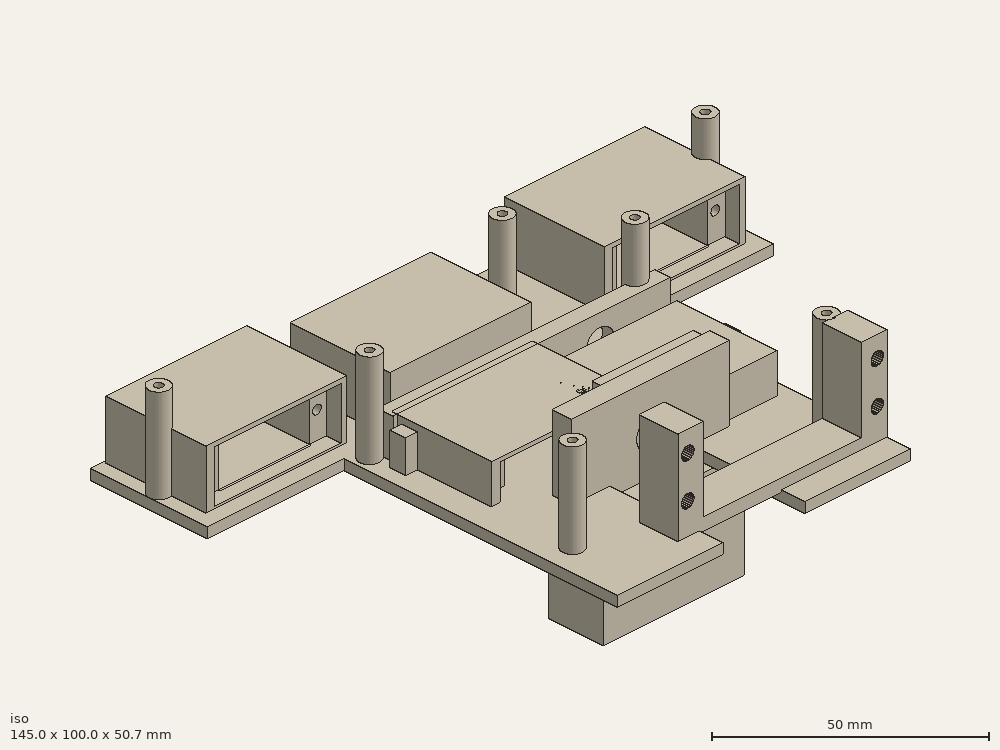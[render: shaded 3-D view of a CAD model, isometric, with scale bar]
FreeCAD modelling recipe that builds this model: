
FCSTD DOCUMENT  (FreeCAD 0.21R33771 (Git))
Label: RobotBrazo
License: All rights reserved
LicenseURL: https://en.wikipedia.org/wiki/All_rights_reserved
objects: PartDesign::Body×27, Sketcher::SketchObject×25, PartDesign::Pad×25, Part::Cut×24, Part::Cylinder×17, Part::MultiFuse×16, Part::FeaturePython×7, Part::Box×6, App::DocumentObjectGroup×5, Part::Feature×3, Mesh::Feature×2, Part::Refine×2, PartDesign::FeatureBase×2, Spreadsheet::Sheet×1
note: 179 computed .brp shape members not serialized (recipe doc carries the construction recipe); baked Part::Feature solids carry a one-line shape summary decoded from their .brp

FEATURE [Mesh::Feature] servo_MG90S
FEATURE [Sketcher::SketchObject] Sketch001
  FullyConstrained = false
  MapMode = 5
  Support = -> [XY_Plane]
  sketch-geometry (4):
    g0: LineSegment StartX=-2.1496 StartY=22.2333 StartZ=0 EndX=33.9123 EndY=22.2333 EndZ=0
    g1: LineSegment StartX=33.9123 StartY=22.2333 StartZ=0 EndX=33.9123 EndY=-3.40604 EndZ=0
    g2: LineSegment StartX=33.9123 StartY=-3.40604 StartZ=0 EndX=-2.1496 EndY=-3.40604 EndZ=0
    g3: LineSegment StartX=-2.1496 StartY=-3.40604 StartZ=0 EndX=-2.1496 EndY=22.2333 EndZ=0
  constraints (8):
    c: Coincident(g0,g1)
    c: Coincident(g1,g2)
    c: Coincident(g2,g3)
    c: Coincident(g3,g0)
    c: Horizontal(g0)
    c: Horizontal(g2)
    c: Vertical(g1)
    c: Vertical(g3)
FEATURE [PartDesign::Pad] Pad
  Direction = (0,0,1)
  Length = 14
  Length2 = 10
  Profile = -> Sketch001
  ReferenceAxis = -> Sketch001 [N_Axis]
  Type = 0
FEATURE [PartDesign::Body] Body  label="Base"
  Group = -> [Sketch001,Pad]
  Origin = -> Origin
  Placement = pos=(0,0,-1) rot=(0,0,1;0rad)
  Tip = -> Pad
FEATURE [Sketcher::SketchObject] Sketch
  FullyConstrained = true
  MapMode = 5
  Placement = pos=(0,0,0) rot=(1,0,0;1.5708rad)
  Support = -> [XZ_Plane003]
  expr: Constraints[10] = Spreadsheet.AnchoCuerpoServo
  expr: Constraints[11] = Spreadsheet.LargoTornillosB
  sketch-geometry (4):
    g0: LineSegment StartX=0 StartY=12.5 StartZ=0 EndX=32.5 EndY=12.5 EndZ=0
    g1: LineSegment StartX=32.5 StartY=12.5 StartZ=0 EndX=32.5 EndY=0 EndZ=0
    g2: LineSegment StartX=32.5 StartY=0 StartZ=0 EndX=0 EndY=0 EndZ=0
    g3: LineSegment StartX=0 StartY=0 StartZ=0 EndX=0 EndY=12.5 EndZ=0
  constraints (12):
    c: Coincident(g0,g1)
    c: Coincident(g1,g2)
    c: Coincident(g2,g3)
    c: Coincident(g3,g0)
    c: Horizontal(g0)
    c: Horizontal(g2)
    c: Vertical(g1)
    c: Vertical(g3)
    c: PointOnObject(g0,g-2)
    c: PointOnObject(g1,g-1)
    c: DistanceY(g1,g1) = 12.5
    c: DistanceX(g0,g0) = 32.5
FEATURE [PartDesign::Pad] Pad001
  Direction = (0,-1,-2e-16)
  Length = 4.5
  Length2 = 10
  Placement = pos=(0,0,0) rot=(1,0,0;1.5708rad)
  Profile = -> Sketch
  ReferenceAxis = -> Sketch [N_Axis]
  Type = 0
  expr: Length = Spreadsheet.AltoServoTor
FEATURE [PartDesign::Body] Body003  label="CorteTornillos"
  Group = -> [Sketch,Pad001]
  Origin = -> Origin003
  Placement = pos=(0,23,0) rot=(0,0,1;0rad)
  Tip = -> Pad001
FEATURE [Part::Cut] Cut  label="BaseCorteTornillos"
  Base = -> Body
  Tool = -> Body003
FEATURE [Sketcher::SketchObject] Sketch002
  FullyConstrained = true
  MapMode = 5
  Placement = pos=(0,0,0) rot=(1,0,0;1.5708rad)
  Support = -> [XZ_Plane004]
  expr: Constraints[10] = Spreadsheet.LargoCuerpoServo
  expr: Constraints[11] = Spreadsheet.DistanciaBaseO
  expr: Constraints[9] = Spreadsheet.AnchoCuerpoServo
  sketch-geometry (4):
    g0: LineSegment StartX=4.75 StartY=12.5 StartZ=0 EndX=28.05 EndY=12.5 EndZ=0
    g1: LineSegment StartX=28.05 StartY=12.5 StartZ=0 EndX=28.05 EndY=0 EndZ=0
    g2: LineSegment StartX=28.05 StartY=0 StartZ=0 EndX=4.75 EndY=0 EndZ=0
    g3: LineSegment StartX=4.75 StartY=0 StartZ=0 EndX=4.75 EndY=12.5 EndZ=0
  constraints (12):
    c: Coincident(g0,g1)
    c: Coincident(g1,g2)
    c: Coincident(g2,g3)
    c: Coincident(g3,g0)
    c: Horizontal(g0)
    c: Horizontal(g2)
    c: Vertical(g1)
    c: Vertical(g3)
    c: PointOnObject(g1,g-1)
    c: DistanceY(g1,g1) = 12.5
    c: DistanceX(g0,g0) = 23.3
    c: DistanceX(g-1,g2) = 4.75
FEATURE [PartDesign::Pad] Pad002
  Direction = (0,-1,-2e-16)
  Length = 19.5
  Length2 = 10
  Placement = pos=(0,0,0) rot=(1,0,0;1.5708rad)
  Profile = -> Sketch002
  ReferenceAxis = -> Sketch002 [N_Axis]
  Type = 0
  expr: Length = Spreadsheet.AltoServo
FEATURE [PartDesign::Body] Body004  label="CorteCuerpo"
  Group = -> [Sketch002,Pad002]
  Origin = -> Origin004
  Placement = pos=(0,19,0) rot=(0,0,1;0rad)
  Tip = -> Pad002
FEATURE [Part::Cut] Cut001  label="SoporteServoMG90S"
  Base = -> Cut
  Tool = -> Body004
FEATURE [Spreadsheet::Sheet] Spreadsheet
  cells = A1='Soporte Servo ; D1='Soporte Servo MG995; A3='AnchoCuerpoServo; B3(AnchoCuerpoServo)=12.5; D3='AnchoCuerpoServo; E3(AnchoCuerpoServoG)=21; A4='LargoCuerpoServo; B4(LargoCuerpoServo)=23.3; D4='LargoCuerpoServo; E4(LargoCuerpoServoG)=40.5; A5='DistanciaBaseO; B5(DistanciaBaseO)=4.75; D5='DistanciaBaseO; E5=4.75; A6='LargoTornillosB; B6(LargoTornillosB)=32.5; D6='LargoTornillosB; E6=32.5; A7='AltoServoTor; B7(AltoServoTor)=4.5; D7='AltoServoTor; E7=4.5; A8='AltoServo; B8(AltoServo)=19.5; D8='AltoServo; E8(AltoServoG)=28; A11='PaloDedoServo; D11='Cuerpo; A12='Largo; B12(PDSLargo)=32; D12='RadioTornillo; E12(CuRadioTornillo)=1; A13='DistaciaCentro; B13(PDSDistanciaCentro)=7; D13='AnchoParedTornillo; E13(CuAnchoParedTornillo)=1.5; A14='DistanciaCurvasPuntas; B14(PDSDistCurvaPunt)=4.5; A15='AnchoPunCen; B15(PDSAnchoPunCen)=6.5; A16='RadioPun; B16(PDSRadioPun)=1.5; A17='Largo Brazo; B17(PDSLargoBrazo)=13; A18='DistaciaComienzoBrazos; B18(PDSDistaComBra)=4.5; A19='DistanciaMitadAlto; B19(PDSDistMidAlto)=3
FEATURE [Part::Cylinder] Cylinder
  Angle = 360
  AttacherType = Attacher::AttachEngine3D
  FirstAngle = 0
  Height = 10
  Placement = pos=(30,22,6) rot=(1,0,0;1.5708rad)
  Radius = 1.1
  SecondAngle = 0
FEATURE [Part::Cylinder] Cylinder001
  Angle = 360
  AttacherType = Attacher::AttachEngine3D
  FirstAngle = 0
  Height = 10
  Placement = pos=(2.2,22,6) rot=(1,0,0;1.5708rad)
  Radius = 1.1
  SecondAngle = 0
FEATURE [Part::MultiFuse] Fusion  label="tornillosSoporteServoHollo"
  Shapes = -> [Cylinder001,Cylinder]
FEATURE [Part::Cut] Cut002  label="SoporteServoCaja"
  Base = -> Cut001
  Placement = pos=(-28.8,27,12) rot=(1,0,0;3.14159rad)
  Tool = -> Fusion
FEATURE [Part::Box] Box  label="Cube"
  AttacherType = Attacher::AttachEngine3D
  Height = 14
  Length = 71
  Placement = pos=(-32,29,-1) rot=(0,0,1;0rad)
  Width = 4
FEATURE [Part::Cylinder] Cylinder004
  Angle = 360
  AttacherType = Attacher::AttachEngine3D
  FirstAngle = 0
  Height = 10
  Placement = pos=(30,22,6) rot=(1,0,0;1.5708rad)
  Radius = 1.1
  SecondAngle = 0
FEATURE [Part::Cylinder] Cylinder005
  Angle = 360
  AttacherType = Attacher::AttachEngine3D
  FirstAngle = 0
  Height = 10
  Placement = pos=(2.2,22,6) rot=(1,0,0;1.5708rad)
  Radius = 1.1
  SecondAngle = 0
FEATURE [Part::MultiFuse] Fusion003  label="tornillosSoporteServoHollo001"
  Shapes = -> [Cylinder005,Cylinder004]
FEATURE [Sketcher::SketchObject] Sketch005
  FullyConstrained = true
  MapMode = 5
  Placement = pos=(0,0,0) rot=(1,0,0;1.5708rad)
  Support = -> [XZ_Plane008]
  expr: Constraints[10] = Spreadsheet.AnchoCuerpoServo
  expr: Constraints[11] = Spreadsheet.LargoTornillosB
  sketch-geometry (4):
    g0: LineSegment StartX=0 StartY=12.5 StartZ=0 EndX=32.5 EndY=12.5 EndZ=0
    g1: LineSegment StartX=32.5 StartY=12.5 StartZ=0 EndX=32.5 EndY=0 EndZ=0
    g2: LineSegment StartX=32.5 StartY=0 StartZ=0 EndX=0 EndY=0 EndZ=0
    g3: LineSegment StartX=0 StartY=0 StartZ=0 EndX=0 EndY=12.5 EndZ=0
  constraints (12):
    c: Coincident(g0,g1)
    c: Coincident(g1,g2)
    c: Coincident(g2,g3)
    c: Coincident(g3,g0)
    c: Horizontal(g0)
    c: Horizontal(g2)
    c: Vertical(g1)
    c: Vertical(g3)
    c: PointOnObject(g0,g-2)
    c: PointOnObject(g1,g-1)
    c: DistanceY(g1,g1) = 12.5
    c: DistanceX(g0,g0) = 32.5
FEATURE [PartDesign::Pad] Pad006
  Direction = (0,-1,-2e-16)
  Length = 4.5
  Length2 = 10
  Placement = pos=(0,0,0) rot=(1,0,0;1.5708rad)
  Profile = -> Sketch005
  ReferenceAxis = -> Sketch005 [N_Axis]
  Type = 0
  expr: Length = Spreadsheet.AltoServoTor
FEATURE [PartDesign::Body] Body008  label="CorteTornillos001"
  Group = -> [Sketch005,Pad006]
  Origin = -> Origin008
  Placement = pos=(0,23,0) rot=(0,0,1;0rad)
  Tip = -> Pad006
FEATURE [Sketcher::SketchObject] Sketch006
  FullyConstrained = false
  MapMode = 5
  Support = -> [XY_Plane007]
  sketch-geometry (4):
    g0: LineSegment StartX=-2.1496 StartY=22.2333 StartZ=0 EndX=33.9123 EndY=22.2333 EndZ=0
    g1: LineSegment StartX=33.9123 StartY=22.2333 StartZ=0 EndX=33.9123 EndY=-3.40604 EndZ=0
    g2: LineSegment StartX=33.9123 StartY=-3.40604 StartZ=0 EndX=-2.1496 EndY=-3.40604 EndZ=0
    g3: LineSegment StartX=-2.1496 StartY=-3.40604 StartZ=0 EndX=-2.1496 EndY=22.2333 EndZ=0
  constraints (8):
    c: Coincident(g0,g1)
    c: Coincident(g1,g2)
    c: Coincident(g2,g3)
    c: Coincident(g3,g0)
    c: Horizontal(g0)
    c: Horizontal(g2)
    c: Vertical(g1)
    c: Vertical(g3)
FEATURE [PartDesign::Pad] Pad005
  Direction = (0,0,1)
  Length = 14
  Length2 = 10
  Profile = -> Sketch006
  ReferenceAxis = -> Sketch006 [N_Axis]
  Type = 0
FEATURE [PartDesign::Body] Body007  label="Base001"
  Group = -> [Sketch006,Pad005]
  Origin = -> Origin007
  Placement = pos=(0,0,-1) rot=(0,0,1;0rad)
  Tip = -> Pad005
FEATURE [Part::Cut] Cut003  label="BaseCorteTornillos001"
  Base = -> Body007
  Tool = -> Body008
FEATURE [Sketcher::SketchObject] Sketch007
  FullyConstrained = true
  MapMode = 5
  Placement = pos=(0,0,0) rot=(1,0,0;1.5708rad)
  Support = -> [XZ_Plane009]
  expr: Constraints[10] = Spreadsheet.LargoCuerpoServo
  expr: Constraints[11] = Spreadsheet.DistanciaBaseO
  expr: Constraints[9] = Spreadsheet.AnchoCuerpoServo
  sketch-geometry (4):
    g0: LineSegment StartX=4.75 StartY=12.5 StartZ=0 EndX=28.05 EndY=12.5 EndZ=0
    g1: LineSegment StartX=28.05 StartY=12.5 StartZ=0 EndX=28.05 EndY=0 EndZ=0
    g2: LineSegment StartX=28.05 StartY=0 StartZ=0 EndX=4.75 EndY=0 EndZ=0
    g3: LineSegment StartX=4.75 StartY=0 StartZ=0 EndX=4.75 EndY=12.5 EndZ=0
  constraints (12):
    c: Coincident(g0,g1)
    c: Coincident(g1,g2)
    c: Coincident(g2,g3)
    c: Coincident(g3,g0)
    c: Horizontal(g0)
    c: Horizontal(g2)
    c: Vertical(g1)
    c: Vertical(g3)
    c: PointOnObject(g1,g-1)
    c: DistanceY(g1,g1) = 12.5
    c: DistanceX(g0,g0) = 23.3
    c: DistanceX(g-1,g2) = 4.75
FEATURE [PartDesign::Pad] Pad007
  Direction = (0,-1,-2e-16)
  Length = 19.5
  Length2 = 10
  Placement = pos=(0,0,0) rot=(1,0,0;1.5708rad)
  Profile = -> Sketch007
  ReferenceAxis = -> Sketch007 [N_Axis]
  Type = 0
  expr: Length = Spreadsheet.AltoServo
FEATURE [PartDesign::Body] Body009  label="CorteCuerpo001"
  Group = -> [Sketch007,Pad007]
  Origin = -> Origin009
  Placement = pos=(0,19,0) rot=(0,0,1;0rad)
  Tip = -> Pad007
FEATURE [Part::Cut] Cut004  label="SoporteServoMG90S001"
  Base = -> Cut003
  Tool = -> Body009
FEATURE [Part::Cylinder] Cylinder006
  Angle = 360
  AttacherType = Attacher::AttachEngine3D
  FirstAngle = 0
  Height = 4
  Placement = pos=(-20,35,6) rot=(0,0.707107,-0.707107;3.14159rad)
  Radius = 5
  SecondAngle = 0
FEATURE [Sketcher::SketchObject] Sketch009
  FullyConstrained = false
  MapMode = 5
  Placement = pos=(0,0,0) rot=(0.57735,0.57735,0.57735;2.0944rad)
  Support = -> [YZ_Plane011]
  sketch-geometry (4):
    g0: LineSegment StartX=24.8013 StartY=11.4231 StartZ=0 EndX=28.8013 EndY=11.4231 EndZ=0
    g1: LineSegment StartX=28.8013 StartY=11.4231 StartZ=0 EndX=28.8013 EndY=0 EndZ=0
    g2: LineSegment StartX=28.8013 StartY=0 StartZ=0 EndX=24.8013 EndY=0 EndZ=0
    g3: LineSegment StartX=24.8013 StartY=0 StartZ=0 EndX=24.8013 EndY=11.4231 EndZ=0
  constraints (10):
    c: Coincident(g0,g1)
    c: Coincident(g1,g2)
    c: Coincident(g2,g3)
    c: Coincident(g3,g0)
    c: Horizontal(g0)
    c: Horizontal(g2)
    c: Vertical(g1)
    c: Vertical(g3)
    c: PointOnObject(g1,g-1)
    c: DistanceX(g2,g2) = 4
FEATURE [PartDesign::Pad] Pad009
  Direction = (1,-2e-16,3e-16)
  Length = 10
  Length2 = 10
  Placement = pos=(0,0,0) rot=(0.57735,0.57735,0.57735;2.0944rad)
  Profile = -> Sketch009
  ReferenceAxis = -> Sketch009 [N_Axis]
  Type = 0
FEATURE [PartDesign::Body] Body011  label="corte cables"
  Group = -> [Sketch009,Pad009]
  Origin = -> Origin011
  Placement = pos=(-34,-1,0) rot=(0,0,1;0rad)
  Tip = -> Pad009
FEATURE [Part::Cut] Cut005  label="SoporteServoCajaMG90S"
  Base = -> Cut004
  Tool = -> Fusion003
FEATURE [App::DocumentObjectGroup] Group002  label="Hombro"
FEATURE [Part::Box] Box001  label="Cube001"
  AttacherType = Attacher::AttachEngine3D
  Height = 14
  Length = 38
  Placement = pos=(0,10,-4) rot=(0,0,1;0rad)
  Width = 4
FEATURE [Part::Cylinder] Cylinder010
  Angle = 360
  AttacherType = Attacher::AttachEngine3D
  FirstAngle = 0
  Height = 8
  Placement = pos=(21,34,6.3) rot=(0.999009,0.030969,-0.031968;1.5708rad)
  Radius = 3.6
  SecondAngle = 0
FEATURE [Sketcher::SketchObject] Sketch013
  FullyConstrained = false
  MapMode = 5
  Placement = pos=(0,0,0) rot=(1,0,0;1.5708rad)
  Support = -> [XZ_Plane015]
  expr: Constraints[13] = Spreadsheet.PDSLargo
  expr: Constraints[20] = Spreadsheet.PDSLargo / 2
  expr: Constraints[25] = Spreadsheet.PDSAnchoPunCen
  sketch-geometry (15):
    g0: GeomPoint X=-8e-15 Y=0.00495753 Z=0
    g1: GeomPoint X=-2.07359 Y=3.25 Z=0
    g2: GeomPoint X=-2.07359 Y=-3.25 Z=0
    g3: GeomPoint X=2.07359 Y=3.25 Z=0
    g4: GeomPoint X=2.07359 Y=-3.25 Z=0
    g5: ArcOfCircle CenterX=-18 CenterY=-1.72e-14 CenterZ=0 NormalX=0 NormalY=0 NormalZ=1 AngleXU=0 Radius=2 StartAngle=1.57081 EndAngle=4.71238
    g6: LineSegment StartX=-18 StartY=2 StartZ=0 EndX=-2.07359 EndY=3.25 EndZ=0
    g7: LineSegment StartX=-18 StartY=-2 StartZ=0 EndX=-2.07359 EndY=-3.25 EndZ=0
    g8: LineSegment StartX=2.07359 StartY=3.25 StartZ=0 EndX=18 EndY=2 EndZ=0
    g9: LineSegment StartX=2.07359 StartY=-3.25 StartZ=0 EndX=18 EndY=-2 EndZ=0
    g10: ArcOfCircle CenterX=18 CenterY=1.72e-14 CenterZ=0 NormalX=0 NormalY=0 NormalZ=1 AngleXU=0 Radius=2 StartAngle=4.7124 EndAngle=7.85397
    g11: ArcOfCircle CenterX=-8e-15 CenterY=0.00495753 CenterZ=0 NormalX=0 NormalY=0 NormalZ=1 AngleXU=0 Radius=3.85934 StartAngle=4.14517 EndAngle=5.27961
    g12: ArcOfCircle CenterX=0 CenterY=0.0440704 CenterZ=0 NormalX=0 NormalY=0 NormalZ=1 AngleXU=0 Radius=3.81808 StartAngle=0.996676 EndAngle=2.14492
    g13: GeomPoint X=-16 Y=0 Z=0
    g14: GeomPoint X=16 Y=-1.65466e-05 Z=0
  constraints (29):
    c: Coincident(g6,g5)
    c: Coincident(g6,g1)
    c: Coincident(g7,g5)
    c: Coincident(g7,g2)
    c: Coincident(g8,g3)
    c: Coincident(g9,g4)
    c: Symmetric(g5,g5,g-1)
    c: Coincident(g10,g8)
    c: Coincident(g10,g9)
    c: Symmetric(g8,g9,g-1)
    c: Equal(g5,g10)
    c: PointOnObject(g13,g5)
    c: PointOnObject(g14,g10)
    c: DistanceX(g13,g14) = 32
    c: Coincident(g8,g12)
    c: Coincident(g1,g12)
    c: Symmetric(g8,g6,g-2)
    c: Coincident(g11,g0)
    c: DistanceY(g9,g8) = 6.5
    c: Radius(g5) = 2
    c: DistanceX(g13,g11) = 16
    c: Coincident(g7,g11)
    c: Coincident(g11,g9)
    c: Symmetric(g7,g9,g-2)
    c: Symmetric(g7,g6,g-1)
    c: DistanceY(g7,g6) = 6.5
    c: DistanceY(g5,g5) = 4
    c: Symmetric(g8,g5,g-2)
    c: PointOnObject(g13,g-1)
FEATURE [PartDesign::Pad] Pad013
  Direction = (0,-1,-2e-16)
  Length = 3
  Length2 = 10
  Placement = pos=(0,0,0) rot=(1,0,0;1.5708rad)
  Profile = -> Sketch013
  ReferenceAxis = -> Sketch013 [N_Axis]
  Type = 0
FEATURE [PartDesign::Body] Body015  label="aggarre004"
  Group = -> [Sketch013,Pad013]
  Origin = -> Origin015
  Placement = pos=(21,35,6.3) rot=(0,0,1;0rad)
  Tip = -> Pad013
FEATURE [Part::MultiFuse] Fusion009  label="ServoAgarre004"
  Shapes = -> [Body015,Cylinder010]
FEATURE [Part::Cut] Cut011
  Base = -> Box
  Tool = -> Cylinder006
FEATURE [Part::Cut] Cut012
  Base = -> Cut011
  Tool = -> Fusion009
FEATURE [Part::MultiFuse] Fusion010
  Shapes = -> [Cut012,Cut002]
FEATURE [App::DocumentObjectGroup] Group  label="GarraSoporte"
  Group = -> [Fusion010,Body011]
FEATURE [Part::Box] Box002  label="Cube002"
  AttacherType = Attacher::AttachEngine3D
  Height = 5
  Length = 38
  Placement = pos=(0,-9,-8) rot=(0,0,1;0rad)
  Width = 23
FEATURE [Sketcher::SketchObject] Sketch016
  FullyConstrained = true
  MapMode = 5
  Support = -> [XY_Plane018]
  sketch-geometry (8):
    g0: LineSegment StartX=-72.5 StartY=36 StartZ=0 EndX=-72.5 EndY=66 EndZ=0
    g1: LineSegment StartX=-72.5 StartY=66 StartZ=0 EndX=72.5 EndY=66 EndZ=0
    g2: LineSegment StartX=72.5 StartY=66 StartZ=0 EndX=72.5 EndY=36 EndZ=0
    g3: LineSegment StartX=-37.5 StartY=36 StartZ=0 EndX=-37.5 EndY=-34 EndZ=0
    g4: LineSegment StartX=-72.5 StartY=36 StartZ=0 EndX=-37.5 EndY=36 EndZ=0
    g5: LineSegment StartX=72.5 StartY=36 StartZ=0 EndX=37.5 EndY=36 EndZ=0
    g6: LineSegment StartX=37.5 StartY=36 StartZ=0 EndX=37.5 EndY=-34 EndZ=0
    g7: LineSegment StartX=-37.5 StartY=-34 StartZ=0 EndX=37.5 EndY=-34 EndZ=0
  constraints (22):
    c: Vertical(g0)
    c: Coincident(g4,g0)
    c: Coincident(g4,g3)
    c: Horizontal(g4)
    c: Horizontal(g5)
    c: Coincident(g6,g5)
    c: Symmetric(g7,g7,g-2)
    c: DistanceY(g2,g2) = 30
    c: Coincident(g6,g7)
    c: Coincident(g3,g7)
    c: DistanceX(g7,g7) = 75
    c: DistanceX(g3,g5) = 75
    c: Symmetric(g5,g3,g-2)
    c: DistanceY(g6,g6) = 70
    c: Equal(g0,g2)
    c: Coincident(g1,g0)
    c: Coincident(g2,g5)
    c: Coincident(g1,g2)
    c: Equal(g5,g4)
    c: DistanceX(g5,g5) = 35
    c: Vertical(g2)
    c: DistanceY(g-1,g0) = 66
FEATURE [PartDesign::Pad] Pad016
  Direction = (0,0,1)
  Length = 2.5
  Length2 = 10
  Profile = -> Sketch016
  ReferenceAxis = -> Sketch016 [N_Axis]
  Type = 0
FEATURE [PartDesign::Body] Body018  label="CuerpoBase"
  Group = -> [Sketch016,Pad016]
  Origin = -> Origin018
  Placement = pos=(0,0,1) rot=(0,0,1;0rad)
  Tip = -> Pad016
FEATURE [Mesh::Feature] ServoGarra_8_  label="ServoGarra(8)"
  Placement = pos=(40,-74,3) rot=(0,0,1;0rad)
FEATURE [Part::Cylinder] Cylinder013
  Angle = 360
  AttacherType = Attacher::AttachEngine3D
  FirstAngle = 0
  Height = 10
  Placement = pos=(30,22,6) rot=(1,0,0;1.5708rad)
  Radius = 1.1
  SecondAngle = 0
FEATURE [Part::Cylinder] Cylinder014
  Angle = 360
  AttacherType = Attacher::AttachEngine3D
  FirstAngle = 0
  Height = 10
  Placement = pos=(2.2,22,6) rot=(1,0,0;1.5708rad)
  Radius = 1.1
  SecondAngle = 0
FEATURE [Part::MultiFuse] Fusion014  label="tornillosSoporteServoHollo002"
  Shapes = -> [Cylinder014,Cylinder013]
FEATURE [Sketcher::SketchObject] Sketch017
  FullyConstrained = true
  MapMode = 5
  Placement = pos=(0,0,0) rot=(1,0,0;1.5708rad)
  Support = -> [XZ_Plane020]
  expr: Constraints[10] = Spreadsheet.AnchoCuerpoServo
  expr: Constraints[11] = Spreadsheet.LargoTornillosB
  sketch-geometry (4):
    g0: LineSegment StartX=0 StartY=12.5 StartZ=0 EndX=32.5 EndY=12.5 EndZ=0
    g1: LineSegment StartX=32.5 StartY=12.5 StartZ=0 EndX=32.5 EndY=0 EndZ=0
    g2: LineSegment StartX=32.5 StartY=0 StartZ=0 EndX=0 EndY=0 EndZ=0
    g3: LineSegment StartX=0 StartY=0 StartZ=0 EndX=0 EndY=12.5 EndZ=0
  constraints (12):
    c: Coincident(g0,g1)
    c: Coincident(g1,g2)
    c: Coincident(g2,g3)
    c: Coincident(g3,g0)
    c: Horizontal(g0)
    c: Horizontal(g2)
    c: Vertical(g1)
    c: Vertical(g3)
    c: PointOnObject(g0,g-2)
    c: PointOnObject(g1,g-1)
    c: DistanceY(g1,g1) = 12.5
    c: DistanceX(g0,g0) = 32.5
FEATURE [PartDesign::Pad] Pad018
  Direction = (0,-1,-2e-16)
  Length = 4.5
  Length2 = 10
  Placement = pos=(0,0,0) rot=(1,0,0;1.5708rad)
  Profile = -> Sketch017
  ReferenceAxis = -> Sketch017 [N_Axis]
  Type = 0
  expr: Length = Spreadsheet.AltoServoTor
FEATURE [PartDesign::Body] Body020  label="CorteTornillos002"
  Group = -> [Sketch017,Pad018]
  Origin = -> Origin020
  Placement = pos=(0,23,0) rot=(0,0,1;0rad)
  Tip = -> Pad018
FEATURE [Sketcher::SketchObject] Sketch018
  FullyConstrained = false
  MapMode = 5
  Support = -> [XY_Plane019]
  sketch-geometry (4):
    g0: LineSegment StartX=-2.1496 StartY=22.2333 StartZ=0 EndX=33.9123 EndY=22.2333 EndZ=0
    g1: LineSegment StartX=33.9123 StartY=22.2333 StartZ=0 EndX=33.9123 EndY=-3.40604 EndZ=0
    g2: LineSegment StartX=33.9123 StartY=-3.40604 StartZ=0 EndX=-2.1496 EndY=-3.40604 EndZ=0
    g3: LineSegment StartX=-2.1496 StartY=-3.40604 StartZ=0 EndX=-2.1496 EndY=22.2333 EndZ=0
  constraints (8):
    c: Coincident(g0,g1)
    c: Coincident(g1,g2)
    c: Coincident(g2,g3)
    c: Coincident(g3,g0)
    c: Horizontal(g0)
    c: Horizontal(g2)
    c: Vertical(g1)
    c: Vertical(g3)
FEATURE [PartDesign::Pad] Pad017
  Direction = (0,0,1)
  Length = 14
  Length2 = 10
  Profile = -> Sketch018
  ReferenceAxis = -> Sketch018 [N_Axis]
  Type = 0
FEATURE [PartDesign::Body] Body019  label="Base002"
  Group = -> [Sketch018,Pad017]
  Origin = -> Origin019
  Placement = pos=(0,0,-1) rot=(0,0,1;0rad)
  Tip = -> Pad017
FEATURE [Part::Cut] Cut014  label="BaseCorteTornillos002"
  Base = -> Body019
  Tool = -> Body020
FEATURE [Sketcher::SketchObject] Sketch019
  FullyConstrained = true
  MapMode = 5
  Placement = pos=(0,0,0) rot=(1,0,0;1.5708rad)
  Support = -> [XZ_Plane021]
  expr: Constraints[10] = Spreadsheet.LargoCuerpoServo
  expr: Constraints[11] = Spreadsheet.DistanciaBaseO
  expr: Constraints[9] = Spreadsheet.AnchoCuerpoServo
  sketch-geometry (4):
    g0: LineSegment StartX=4.75 StartY=12.5 StartZ=0 EndX=28.05 EndY=12.5 EndZ=0
    g1: LineSegment StartX=28.05 StartY=12.5 StartZ=0 EndX=28.05 EndY=0 EndZ=0
    g2: LineSegment StartX=28.05 StartY=0 StartZ=0 EndX=4.75 EndY=0 EndZ=0
    g3: LineSegment StartX=4.75 StartY=0 StartZ=0 EndX=4.75 EndY=12.5 EndZ=0
  constraints (12):
    c: Coincident(g0,g1)
    c: Coincident(g1,g2)
    c: Coincident(g2,g3)
    c: Coincident(g3,g0)
    c: Horizontal(g0)
    c: Horizontal(g2)
    c: Vertical(g1)
    c: Vertical(g3)
    c: PointOnObject(g1,g-1)
    c: DistanceY(g1,g1) = 12.5
    c: DistanceX(g0,g0) = 23.3
    c: DistanceX(g-1,g2) = 4.75
FEATURE [PartDesign::Pad] Pad019
  Direction = (0,-1,-2e-16)
  Length = 19.5
  Length2 = 10
  Placement = pos=(0,0,0) rot=(1,0,0;1.5708rad)
  Profile = -> Sketch019
  ReferenceAxis = -> Sketch019 [N_Axis]
  Type = 0
  expr: Length = Spreadsheet.AltoServo
FEATURE [PartDesign::Body] Body021  label="CorteCuerpo002"
  Group = -> [Sketch019,Pad019]
  Origin = -> Origin021
  Placement = pos=(0,19,0) rot=(0,0,1;0rad)
  Tip = -> Pad019
FEATURE [Part::Cut] Cut015  label="SoporteServoMG90S002"
  Base = -> Cut014
  Tool = -> Body021
FEATURE [Part::Cut] Cut016  label="SoporteServoCajaMG90S001"
  Base = -> Cut015
  Placement = pos=(-24,39,4) rot=(0,0,1;0rad)
  Tool = -> Fusion014
FEATURE [Part::Cylinder] Cylinder015
  Angle = 360
  AttacherType = Attacher::AttachEngine3D
  FirstAngle = 0
  Height = 10
  Placement = pos=(30,22,6) rot=(1,0,0;1.5708rad)
  Radius = 1.1
  SecondAngle = 0
FEATURE [Part::Cylinder] Cylinder016
  Angle = 360
  AttacherType = Attacher::AttachEngine3D
  FirstAngle = 0
  Height = 10
  Placement = pos=(2.2,22,6) rot=(1,0,0;1.5708rad)
  Radius = 1.1
  SecondAngle = 0
FEATURE [Part::MultiFuse] Fusion015  label="tornillosSoporteServoHollo003"
  Shapes = -> [Cylinder016,Cylinder015]
FEATURE [Sketcher::SketchObject] Sketch020
  FullyConstrained = true
  MapMode = 5
  Placement = pos=(0,0,0) rot=(1,0,0;1.5708rad)
  Support = -> [XZ_Plane023]
  expr: Constraints[10] = Spreadsheet.AnchoCuerpoServo
  expr: Constraints[11] = Spreadsheet.LargoTornillosB
  sketch-geometry (4):
    g0: LineSegment StartX=0 StartY=12.5 StartZ=0 EndX=32.5 EndY=12.5 EndZ=0
    g1: LineSegment StartX=32.5 StartY=12.5 StartZ=0 EndX=32.5 EndY=0 EndZ=0
    g2: LineSegment StartX=32.5 StartY=0 StartZ=0 EndX=0 EndY=0 EndZ=0
    g3: LineSegment StartX=0 StartY=0 StartZ=0 EndX=0 EndY=12.5 EndZ=0
  constraints (12):
    c: Coincident(g0,g1)
    c: Coincident(g1,g2)
    c: Coincident(g2,g3)
    c: Coincident(g3,g0)
    c: Horizontal(g0)
    c: Horizontal(g2)
    c: Vertical(g1)
    c: Vertical(g3)
    c: PointOnObject(g0,g-2)
    c: PointOnObject(g1,g-1)
    c: DistanceY(g1,g1) = 12.5
    c: DistanceX(g0,g0) = 32.5
FEATURE [PartDesign::Pad] Pad021
  Direction = (0,-1,-2e-16)
  Length = 4.5
  Length2 = 10
  Placement = pos=(0,0,0) rot=(1,0,0;1.5708rad)
  Profile = -> Sketch020
  ReferenceAxis = -> Sketch020 [N_Axis]
  Type = 0
  expr: Length = Spreadsheet.AltoServoTor
FEATURE [PartDesign::Body] Body023  label="CorteTornillos003"
  Group = -> [Sketch020,Pad021]
  Origin = -> Origin023
  Placement = pos=(0,23,0) rot=(0,0,1;0rad)
  Tip = -> Pad021
FEATURE [Sketcher::SketchObject] Sketch021
  FullyConstrained = false
  MapMode = 5
  Support = -> [XY_Plane022]
  sketch-geometry (4):
    g0: LineSegment StartX=-2.1496 StartY=22.2333 StartZ=0 EndX=33.9123 EndY=22.2333 EndZ=0
    g1: LineSegment StartX=33.9123 StartY=22.2333 StartZ=0 EndX=33.9123 EndY=-3.40604 EndZ=0
    g2: LineSegment StartX=33.9123 StartY=-3.40604 StartZ=0 EndX=-2.1496 EndY=-3.40604 EndZ=0
    g3: LineSegment StartX=-2.1496 StartY=-3.40604 StartZ=0 EndX=-2.1496 EndY=22.2333 EndZ=0
  constraints (8):
    c: Coincident(g0,g1)
    c: Coincident(g1,g2)
    c: Coincident(g2,g3)
    c: Coincident(g3,g0)
    c: Horizontal(g0)
    c: Horizontal(g2)
    c: Vertical(g1)
    c: Vertical(g3)
FEATURE [PartDesign::Pad] Pad020
  Direction = (0,0,1)
  Length = 14
  Length2 = 10
  Profile = -> Sketch021
  ReferenceAxis = -> Sketch021 [N_Axis]
  Type = 0
FEATURE [PartDesign::Body] Body022  label="Base003"
  Group = -> [Sketch021,Pad020]
  Origin = -> Origin022
  Placement = pos=(0,0,-1) rot=(0,0,1;0rad)
  Tip = -> Pad020
FEATURE [Part::Cut] Cut017  label="BaseCorteTornillos003"
  Base = -> Body022
  Tool = -> Body023
FEATURE [Sketcher::SketchObject] Sketch022
  FullyConstrained = true
  MapMode = 5
  Placement = pos=(0,0,0) rot=(1,0,0;1.5708rad)
  Support = -> [XZ_Plane024]
  expr: Constraints[10] = Spreadsheet.LargoCuerpoServo
  expr: Constraints[11] = Spreadsheet.DistanciaBaseO
  expr: Constraints[9] = Spreadsheet.AnchoCuerpoServo
  sketch-geometry (4):
    g0: LineSegment StartX=4.75 StartY=12.5 StartZ=0 EndX=28.05 EndY=12.5 EndZ=0
    g1: LineSegment StartX=28.05 StartY=12.5 StartZ=0 EndX=28.05 EndY=0 EndZ=0
    g2: LineSegment StartX=28.05 StartY=0 StartZ=0 EndX=4.75 EndY=0 EndZ=0
    g3: LineSegment StartX=4.75 StartY=0 StartZ=0 EndX=4.75 EndY=12.5 EndZ=0
  constraints (12):
    c: Coincident(g0,g1)
    c: Coincident(g1,g2)
    c: Coincident(g2,g3)
    c: Coincident(g3,g0)
    c: Horizontal(g0)
    c: Horizontal(g2)
    c: Vertical(g1)
    c: Vertical(g3)
    c: PointOnObject(g1,g-1)
    c: DistanceY(g1,g1) = 12.5
    c: DistanceX(g0,g0) = 23.3
    c: DistanceX(g-1,g2) = 4.75
FEATURE [PartDesign::Pad] Pad022
  Direction = (0,-1,-2e-16)
  Length = 19.5
  Length2 = 10
  Placement = pos=(0,0,0) rot=(1,0,0;1.5708rad)
  Profile = -> Sketch022
  ReferenceAxis = -> Sketch022 [N_Axis]
  Type = 0
  expr: Length = Spreadsheet.AltoServo
FEATURE [PartDesign::Body] Body024  label="CorteCuerpo003"
  Group = -> [Sketch022,Pad022]
  Origin = -> Origin024
  Placement = pos=(0,19,0) rot=(0,0,1;0rad)
  Tip = -> Pad022
FEATURE [Part::Cut] Cut018  label="SoporteServoMG90S003"
  Base = -> Cut017
  Tool = -> Body024
FEATURE [Part::Cut] Cut019  label="SoporteServoCajaMG90S002"
  Base = -> Cut018
  Placement = pos=(-67,62,16.5) rot=(1,0,0;3.14159rad)
  Tool = -> Fusion015
FEATURE [Part::Cylinder] Cylinder017
  Angle = 360
  AttacherType = Attacher::AttachEngine3D
  FirstAngle = 0
  Height = 10
  Placement = pos=(30,22,6) rot=(1,0,0;1.5708rad)
  Radius = 1.1
  SecondAngle = 0
FEATURE [Part::Cylinder] Cylinder018
  Angle = 360
  AttacherType = Attacher::AttachEngine3D
  FirstAngle = 0
  Height = 10
  Placement = pos=(2.2,22,6) rot=(1,0,0;1.5708rad)
  Radius = 1.1
  SecondAngle = 0
FEATURE [Part::MultiFuse] Fusion016  label="tornillosSoporteServoHollo004"
  Shapes = -> [Cylinder018,Cylinder017]
FEATURE [Sketcher::SketchObject] Sketch023
  FullyConstrained = true
  MapMode = 5
  Placement = pos=(0,0,0) rot=(1,0,0;1.5708rad)
  Support = -> [XZ_Plane026]
  expr: Constraints[10] = Spreadsheet.AnchoCuerpoServo
  expr: Constraints[11] = Spreadsheet.LargoTornillosB
  sketch-geometry (4):
    g0: LineSegment StartX=0 StartY=12.5 StartZ=0 EndX=32.5 EndY=12.5 EndZ=0
    g1: LineSegment StartX=32.5 StartY=12.5 StartZ=0 EndX=32.5 EndY=0 EndZ=0
    g2: LineSegment StartX=32.5 StartY=0 StartZ=0 EndX=0 EndY=0 EndZ=0
    g3: LineSegment StartX=0 StartY=0 StartZ=0 EndX=0 EndY=12.5 EndZ=0
  constraints (12):
    c: Coincident(g0,g1)
    c: Coincident(g1,g2)
    c: Coincident(g2,g3)
    c: Coincident(g3,g0)
    c: Horizontal(g0)
    c: Horizontal(g2)
    c: Vertical(g1)
    c: Vertical(g3)
    c: PointOnObject(g0,g-2)
    c: PointOnObject(g1,g-1)
    c: DistanceY(g1,g1) = 12.5
    c: DistanceX(g0,g0) = 32.5
FEATURE [PartDesign::Pad] Pad024
  Direction = (0,-1,-2e-16)
  Length = 4.5
  Length2 = 10
  Placement = pos=(0,0,0) rot=(1,0,0;1.5708rad)
  Profile = -> Sketch023
  ReferenceAxis = -> Sketch023 [N_Axis]
  Type = 0
  expr: Length = Spreadsheet.AltoServoTor
FEATURE [PartDesign::Body] Body026  label="CorteTornillos004"
  Group = -> [Sketch023,Pad024]
  Origin = -> Origin026
  Placement = pos=(0,23,0) rot=(0,0,1;0rad)
  Tip = -> Pad024
FEATURE [Sketcher::SketchObject] Sketch024
  FullyConstrained = false
  MapMode = 5
  Support = -> [XY_Plane025]
  sketch-geometry (4):
    g0: LineSegment StartX=-2.1496 StartY=22.2333 StartZ=0 EndX=33.9123 EndY=22.2333 EndZ=0
    g1: LineSegment StartX=33.9123 StartY=22.2333 StartZ=0 EndX=33.9123 EndY=-3.40604 EndZ=0
    g2: LineSegment StartX=33.9123 StartY=-3.40604 StartZ=0 EndX=-2.1496 EndY=-3.40604 EndZ=0
    g3: LineSegment StartX=-2.1496 StartY=-3.40604 StartZ=0 EndX=-2.1496 EndY=22.2333 EndZ=0
  constraints (8):
    c: Coincident(g0,g1)
    c: Coincident(g1,g2)
    c: Coincident(g2,g3)
    c: Coincident(g3,g0)
    c: Horizontal(g0)
    c: Horizontal(g2)
    c: Vertical(g1)
    c: Vertical(g3)
FEATURE [PartDesign::Pad] Pad023
  Direction = (0,0,1)
  Length = 14
  Length2 = 10
  Profile = -> Sketch024
  ReferenceAxis = -> Sketch024 [N_Axis]
  Type = 0
FEATURE [PartDesign::Body] Body025  label="Base004"
  Group = -> [Sketch024,Pad023]
  Origin = -> Origin025
  Placement = pos=(0,0,-1) rot=(0,0,1;0rad)
  Tip = -> Pad023
FEATURE [Part::Cut] Cut020  label="BaseCorteTornillos004"
  Base = -> Body025
  Tool = -> Body026
FEATURE [Sketcher::SketchObject] Sketch025
  FullyConstrained = true
  MapMode = 5
  Placement = pos=(0,0,0) rot=(1,0,0;1.5708rad)
  Support = -> [XZ_Plane027]
  expr: Constraints[10] = Spreadsheet.LargoCuerpoServo
  expr: Constraints[11] = Spreadsheet.DistanciaBaseO
  expr: Constraints[9] = Spreadsheet.AnchoCuerpoServo
  sketch-geometry (4):
    g0: LineSegment StartX=4.75 StartY=12.5 StartZ=0 EndX=28.05 EndY=12.5 EndZ=0
    g1: LineSegment StartX=28.05 StartY=12.5 StartZ=0 EndX=28.05 EndY=0 EndZ=0
    g2: LineSegment StartX=28.05 StartY=0 StartZ=0 EndX=4.75 EndY=0 EndZ=0
    g3: LineSegment StartX=4.75 StartY=0 StartZ=0 EndX=4.75 EndY=12.5 EndZ=0
  constraints (12):
    c: Coincident(g0,g1)
    c: Coincident(g1,g2)
    c: Coincident(g2,g3)
    c: Coincident(g3,g0)
    c: Horizontal(g0)
    c: Horizontal(g2)
    c: Vertical(g1)
    c: Vertical(g3)
    c: PointOnObject(g1,g-1)
    c: DistanceY(g1,g1) = 12.5
    c: DistanceX(g0,g0) = 23.3
    c: DistanceX(g-1,g2) = 4.75
FEATURE [PartDesign::Pad] Pad025
  Direction = (0,-1,-2e-16)
  Length = 19.5
  Length2 = 10
  Placement = pos=(0,0,0) rot=(1,0,0;1.5708rad)
  Profile = -> Sketch025
  ReferenceAxis = -> Sketch025 [N_Axis]
  Type = 0
  expr: Length = Spreadsheet.AltoServo
FEATURE [PartDesign::Body] Body027  label="CorteCuerpo004"
  Group = -> [Sketch025,Pad025]
  Origin = -> Origin027
  Placement = pos=(0,19,0) rot=(0,0,1;0rad)
  Tip = -> Pad025
FEATURE [Part::Cut] Cut021  label="SoporteServoMG90S004"
  Base = -> Cut020
  Tool = -> Body027
FEATURE [Part::Cut] Cut022  label="SoporteServoCajaMG90S003"
  Base = -> Cut021
  Placement = pos=(35,62,16.5) rot=(1,0,0;3.14159rad)
  Tool = -> Fusion016
FEATURE [Part::Feature] ServoGarra_8_001
  shape: bbox 53.5 x 10 x 23 mm, 482 faces, 0 solids (baked)
FEATURE [Part::Feature] ServoGarra_8_001_solid  label="ServoGarra_8_001 (Solid)"
  shape: bbox 53.5 x 10 x 23 mm, 482 faces (baked)
FEATURE [Part::Refine] ServoGarra_8_001_solid001  label="ServoGarra_8_001 (Solid)001"
  Source = -> ServoGarra_8_001_solid
FEATURE [PartDesign::FeatureBase] BaseFeature
  BaseFeature = -> ServoGarra_8_001_solid001
FEATURE [PartDesign::Body] Body028  label="Body"
  BaseFeature = -> ServoGarra_8_001_solid001
  Group = -> [BaseFeature]
  Origin = -> Origin028
  Placement = pos=(4.5,0,0) rot=(0,0,1;0rad)
  Tip = -> BaseFeature
FEATURE [Part::Box] Box004  label="Cube004"
  AttacherType = Attacher::AttachEngine3D
  Height = 5
  Length = 26
  Placement = pos=(0,-9,-8) rot=(0,0,1;0rad)
  Width = 19
FEATURE [Part::Cylinder] Cylinder020
  Angle = 360
  AttacherType = Attacher::AttachEngine3D
  FirstAngle = 0
  Height = 8
  Placement = pos=(21,34,6) rot=(0.999009,0.030969,-0.031968;1.5708rad)
  Radius = 3.7
  SecondAngle = 0
FEATURE [Sketcher::SketchObject] Sketch027
  FullyConstrained = false
  MapMode = 5
  Placement = pos=(0,0,0) rot=(1,0,0;1.5708rad)
  Support = -> [XZ_Plane030]
  sketch-geometry (11):
    g0: GeomPoint X=-0.0034459 Y=-1.081e-13 Z=0
    g1: GeomPoint X=-3.70949 Y=6.07857e-05 Z=0
    g2: GeomPoint X=2.27101 Y=2.90605 Z=0
    g3: GeomPoint X=2.22423 Y=-3 Z=0
    g4: LineSegment StartX=2.27101 StartY=2.90605 StartZ=0 EndX=15.2241 EndY=2.17981 EndZ=0
    g5: LineSegment StartX=2.22423 StartY=-3 StartZ=0 EndX=15.2241 EndY=-2.17981 EndZ=0
    g6: ArcOfCircle CenterX=14 CenterY=-4e-16 CenterZ=0 NormalX=0 NormalY=0 NormalZ=1 AngleXU=0 Radius=2.5 StartAngle=5.22407 EndAngle=7.3423
    g7: ArcOfCircle CenterX=-0.0034459 CenterY=-1.081e-13 CenterZ=0 NormalX=0 NormalY=0 NormalZ=1 AngleXU=0 Radius=3.73665 StartAngle=3.14158 EndAngle=5.35111
    g8: ArcOfCircle CenterX=-0.0131859 CenterY=3.19156e-06 CenterZ=0 NormalX=0 NormalY=0 NormalZ=1 AngleXU=0 Radius=3.6963 StartAngle=0.904641 EndAngle=3.14158
    g9: GeomPoint X=16.5 Y=-3.68e-14 Z=0
    g10: LineSegment StartX=-3.70949 StartY=6.07857e-05 StartZ=0 EndX=-3.74009 EndY=6.07857e-05 EndZ=0
  constraints (14):
    c: Coincident(g4,g2)
    c: Coincident(g5,g3)
    c: Coincident(g6,g4)
    c: Coincident(g6,g5)
    c: Symmetric(g4,g5,g-1)
    c: PointOnObject(g9,g6)
    c: Coincident(g1,g8)
    c: Coincident(g7,g0)
    c: DistanceY(g5,g4) = 5.90605
    c: Coincident(g10,g8)
    c: Coincident(g10,g7)
    c: Horizontal(g10)
    c: Coincident(g7,g5)
    c: Coincident(g4,g8)
FEATURE [PartDesign::Pad] Pad027
  Direction = (0,-1,-2e-16)
  Length = 4
  Length2 = 10
  Placement = pos=(0,0,0) rot=(1,0,0;1.5708rad)
  Profile = -> Sketch027
  ReferenceAxis = -> Sketch027 [N_Axis]
  Type = 0
FEATURE [PartDesign::Body] Body030  label="aggarre008"
  Group = -> [Sketch027,Pad027]
  Origin = -> Origin030
  Placement = pos=(21,34,6) rot=(0,0,1;0rad)
  Tip = -> Pad027
FEATURE [Part::MultiFuse] Fusion019  label="ServoAgarre008"
  Placement = pos=(40,-8,-37) rot=(0,0.707107,0.707107;3.14159rad)
  Shapes = -> [Body030,Cylinder020]
FEATURE [Part::Cut] Cut024
  Base = -> Box004
  Tool = -> Fusion019
FEATURE [Part::Box] Box005  label="Cube005"
  AttacherType = Attacher::AttachEngine3D
  Height = 5
  Length = 26
  Placement = pos=(0,-9,-8) rot=(0,0,1;0rad)
  Width = 23
FEATURE [Part::Cylinder] Cylinder021
  Angle = 360
  AttacherType = Attacher::AttachEngine3D
  FirstAngle = 0
  Height = 8
  Placement = pos=(21,34,6) rot=(0.999009,0.030969,-0.031968;1.5708rad)
  Radius = 3.7
  SecondAngle = 0
FEATURE [Sketcher::SketchObject] Sketch028
  FullyConstrained = false
  MapMode = 5
  Placement = pos=(0,0,0) rot=(1,0,0;1.5708rad)
  Support = -> [XZ_Plane031]
  sketch-geometry (11):
    g0: GeomPoint X=-0.0034459 Y=-1.081e-13 Z=0
    g1: GeomPoint X=-3.70949 Y=6.07857e-05 Z=0
    g2: GeomPoint X=2.27101 Y=2.90605 Z=0
    g3: GeomPoint X=2.22423 Y=-3 Z=0
    g4: LineSegment StartX=2.27101 StartY=2.90605 StartZ=0 EndX=15.2241 EndY=2.17981 EndZ=0
    g5: LineSegment StartX=2.22423 StartY=-3 StartZ=0 EndX=15.2241 EndY=-2.17981 EndZ=0
    g6: ArcOfCircle CenterX=14 CenterY=-4e-16 CenterZ=0 NormalX=0 NormalY=0 NormalZ=1 AngleXU=0 Radius=2.5 StartAngle=5.22407 EndAngle=7.3423
    g7: ArcOfCircle CenterX=-0.0034459 CenterY=-1.081e-13 CenterZ=0 NormalX=0 NormalY=0 NormalZ=1 AngleXU=0 Radius=3.73665 StartAngle=3.14158 EndAngle=5.35111
    g8: ArcOfCircle CenterX=-0.0131859 CenterY=3.19156e-06 CenterZ=0 NormalX=0 NormalY=0 NormalZ=1 AngleXU=0 Radius=3.6963 StartAngle=0.904641 EndAngle=3.14158
    g9: GeomPoint X=16.5 Y=-3.68e-14 Z=0
    g10: LineSegment StartX=-3.70949 StartY=6.07857e-05 StartZ=0 EndX=-3.74009 EndY=6.07857e-05 EndZ=0
  constraints (14):
    c: Coincident(g4,g2)
    c: Coincident(g5,g3)
    c: Coincident(g6,g4)
    c: Coincident(g6,g5)
    c: Symmetric(g4,g5,g-1)
    c: PointOnObject(g9,g6)
    c: Coincident(g1,g8)
    c: Coincident(g7,g0)
    c: DistanceY(g5,g4) = 5.90605
    c: Coincident(g10,g8)
    c: Coincident(g10,g7)
    c: Horizontal(g10)
    c: Coincident(g7,g5)
    c: Coincident(g4,g8)
FEATURE [PartDesign::Pad] Pad028
  Direction = (0,-1,-2e-16)
  Length = 4
  Length2 = 10
  Placement = pos=(0,0,0) rot=(1,0,0;1.5708rad)
  Profile = -> Sketch028
  ReferenceAxis = -> Sketch028 [N_Axis]
  Type = 0
FEATURE [PartDesign::Body] Body031  label="aggarre009"
  Group = -> [Sketch028,Pad028]
  Origin = -> Origin031
  Placement = pos=(21,34,6) rot=(0,0,1;0rad)
  Tip = -> Pad028
FEATURE [Part::MultiFuse] Fusion020  label="ServoAgarre009"
  Placement = pos=(40,-8,-37) rot=(0,0.707107,0.707107;3.14159rad)
  Shapes = -> [Body031,Cylinder021]
FEATURE [Part::Cut] Cut025
  Base = -> Box005
  Placement = pos=(26,2,6) rot=(0,0.707107,-0.707107;3.14159rad)
  Tool = -> Fusion020
FEATURE [Part::MultiFuse] Fusion021
  Shapes = -> [Cut024,Cut025]
FEATURE [Part::MultiFuse] Fusion022
  Shapes = -> [Body018,Cut016,Cut019,Cut022]
FEATURE [Part::FeaturePython] Tube  # WARN: FeaturePython — macro-defined, semantics opaque (R4)
  AttacherType = Attacher::AttachEngine3D
  Height = 24
  InnerRadius = 1
  OuterRadius = 2.5
  Placement = pos=(34,-16,2) rot=(0,0,1;0rad)
  expr: InnerRadius = Spreadsheet.CuRadioTornillo
  expr: OuterRadius = Spreadsheet.CuRadioTornillo + Spreadsheet.CuAnchoParedTornillo
FEATURE [Part::FeaturePython] Tube001  # WARN: FeaturePython — macro-defined, semantics opaque (R4)
  AttacherType = Attacher::AttachEngine3D
  Height = 24
  InnerRadius = 1
  OuterRadius = 2.5
  Placement = pos=(-31,-16,2) rot=(0,0,1;0rad)
  expr: InnerRadius = Spreadsheet.CuRadioTornillo
  expr: OuterRadius = Spreadsheet.CuRadioTornillo + Spreadsheet.CuAnchoParedTornillo
FEATURE [Part::FeaturePython] Tube002  # WARN: FeaturePython — macro-defined, semantics opaque (R4)
  AttacherType = Attacher::AttachEngine3D
  Height = 24
  InnerRadius = 1
  OuterRadius = 2.5
  Placement = pos=(34,33,2) rot=(0,0,1;0rad)
  expr: InnerRadius = Spreadsheet.CuRadioTornillo
  expr: OuterRadius = Spreadsheet.CuRadioTornillo + Spreadsheet.CuAnchoParedTornillo
FEATURE [Part::FeaturePython] Tube003  # WARN: FeaturePython — macro-defined, semantics opaque (R4)
  AttacherType = Attacher::AttachEngine3D
  Height = 24
  InnerRadius = 1
  OuterRadius = 2.5
  Placement = pos=(-34,33,2) rot=(0,0,1;0rad)
  expr: InnerRadius = Spreadsheet.CuRadioTornillo
  expr: OuterRadius = Spreadsheet.CuRadioTornillo + Spreadsheet.CuAnchoParedTornillo
FEATURE [Part::FeaturePython] Tube004  # WARN: FeaturePython — macro-defined, semantics opaque (R4)
  AttacherType = Attacher::AttachEngine3D
  Height = 24
  InnerRadius = 1
  OuterRadius = 2.5
  Placement = pos=(70,51,2) rot=(0,0,1;0rad)
  expr: InnerRadius = Spreadsheet.CuRadioTornillo
  expr: OuterRadius = Spreadsheet.CuRadioTornillo + Spreadsheet.CuAnchoParedTornillo
FEATURE [Part::FeaturePython] Tube005  # WARN: FeaturePython — macro-defined, semantics opaque (R4)
  AttacherType = Attacher::AttachEngine3D
  Height = 24
  InnerRadius = 1
  OuterRadius = 2.5
  Placement = pos=(-70,51,2) rot=(0,0,1;0rad)
  expr: InnerRadius = Spreadsheet.CuRadioTornillo
  expr: OuterRadius = Spreadsheet.CuRadioTornillo + Spreadsheet.CuAnchoParedTornillo
FEATURE [Part::FeaturePython] Tube006  # WARN: FeaturePython — macro-defined, semantics opaque (R4)
  AttacherType = Attacher::AttachEngine3D
  Height = 24
  InnerRadius = 1
  OuterRadius = 2.5
  Placement = pos=(18,51,2) rot=(0,0,1;0rad)
  expr: InnerRadius = Spreadsheet.CuRadioTornillo
  expr: OuterRadius = Spreadsheet.CuRadioTornillo + Spreadsheet.CuAnchoParedTornillo
FEATURE [Part::MultiFuse] Fusion023  label="Tornillos"
  Shapes = -> [Tube006,Tube,Tube001,Tube002,Tube003,Tube004,Tube005]
FEATURE [Part::MultiFuse] Fusion024
  Shapes = -> [Box002,Box001]
FEATURE [App::DocumentObjectGroup] Group001  label="utils"
  Group = -> [Cut005,servo_MG90S,ServoGarra_8_,Fusion021,Body028,ServoGarra_8_001,ServoGarra_8_001_solid,ServoGarra_8_001_solid001,Fusion024]
FEATURE [Part::Cylinder] Cylinder023
  Angle = 360
  AttacherType = Attacher::AttachEngine3D
  FirstAngle = 0
  Height = 8
  Placement = pos=(21,34,6.3) rot=(0.999009,0.030969,-0.031968;1.5708rad)
  Radius = 3.6
  SecondAngle = 0
FEATURE [Sketcher::SketchObject] Sketch031
  FullyConstrained = false
  MapMode = 5
  Placement = pos=(0,0,0) rot=(1,0,0;1.5708rad)
  Support = -> [XZ_Plane034]
  expr: Constraints[13] = Spreadsheet.PDSLargo
  expr: Constraints[20] = Spreadsheet.PDSLargo / 2
  expr: Constraints[25] = Spreadsheet.PDSAnchoPunCen
  sketch-geometry (15):
    g0: GeomPoint X=-8e-15 Y=0.00495753 Z=0
    g1: GeomPoint X=-2.07359 Y=3.25 Z=0
    g2: GeomPoint X=-2.07359 Y=-3.25 Z=0
    g3: GeomPoint X=2.07359 Y=3.25 Z=0
    g4: GeomPoint X=2.07359 Y=-3.25 Z=0
    g5: ArcOfCircle CenterX=-18 CenterY=-1.72e-14 CenterZ=0 NormalX=0 NormalY=0 NormalZ=1 AngleXU=0 Radius=2 StartAngle=1.57081 EndAngle=4.71238
    g6: LineSegment StartX=-18 StartY=2 StartZ=0 EndX=-2.07359 EndY=3.25 EndZ=0
    g7: LineSegment StartX=-18 StartY=-2 StartZ=0 EndX=-2.07359 EndY=-3.25 EndZ=0
    g8: LineSegment StartX=2.07359 StartY=3.25 StartZ=0 EndX=18 EndY=2 EndZ=0
    g9: LineSegment StartX=2.07359 StartY=-3.25 StartZ=0 EndX=18 EndY=-2 EndZ=0
    g10: ArcOfCircle CenterX=18 CenterY=1.72e-14 CenterZ=0 NormalX=0 NormalY=0 NormalZ=1 AngleXU=0 Radius=2 StartAngle=4.7124 EndAngle=7.85397
    g11: ArcOfCircle CenterX=-8e-15 CenterY=0.00495753 CenterZ=0 NormalX=0 NormalY=0 NormalZ=1 AngleXU=0 Radius=3.85934 StartAngle=4.14517 EndAngle=5.27961
    g12: ArcOfCircle CenterX=0 CenterY=0.0440704 CenterZ=0 NormalX=0 NormalY=0 NormalZ=1 AngleXU=0 Radius=3.81808 StartAngle=0.996676 EndAngle=2.14492
    g13: GeomPoint X=-16 Y=0 Z=0
    g14: GeomPoint X=16 Y=-1.65466e-05 Z=0
  constraints (29):
    c: Coincident(g6,g5)
    c: Coincident(g6,g1)
    c: Coincident(g7,g5)
    c: Coincident(g7,g2)
    c: Coincident(g8,g3)
    c: Coincident(g9,g4)
    c: Symmetric(g5,g5,g-1)
    c: Coincident(g10,g8)
    c: Coincident(g10,g9)
    c: Symmetric(g8,g9,g-1)
    c: Equal(g5,g10)
    c: PointOnObject(g13,g5)
    c: PointOnObject(g14,g10)
    c: DistanceX(g13,g14) = 32
    c: Coincident(g8,g12)
    c: Coincident(g1,g12)
    c: Symmetric(g8,g6,g-2)
    c: Coincident(g11,g0)
    c: DistanceY(g9,g8) = 6.5
    c: Radius(g5) = 2
    c: DistanceX(g13,g11) = 16
    c: Coincident(g7,g11)
    c: Coincident(g11,g9)
    c: Symmetric(g7,g9,g-2)
    c: Symmetric(g7,g6,g-1)
    c: DistanceY(g7,g6) = 6.5
    c: DistanceY(g5,g5) = 4
    c: Symmetric(g8,g5,g-2)
    c: PointOnObject(g13,g-1)
FEATURE [PartDesign::Pad] Pad031
  Direction = (0,-1,-2e-16)
  Length = 3
  Length2 = 10
  Placement = pos=(0,0,0) rot=(1,0,0;1.5708rad)
  Profile = -> Sketch031
  ReferenceAxis = -> Sketch031 [N_Axis]
  Type = 0
FEATURE [PartDesign::Body] Body034  label="aggarre011"
  Group = -> [Sketch031,Pad031]
  Origin = -> Origin034
  Placement = pos=(21,35,6.3) rot=(0,0,1;0rad)
  Tip = -> Pad031
FEATURE [Part::MultiFuse] Fusion026  label="ServoAgarre011"
  Placement = pos=(-21,-35,4) rot=(0,0,1;0rad)
  Shapes = -> [Body034,Cylinder023]
FEATURE [Sketcher::SketchObject] Sketch032
  FullyConstrained = false
  MapMode = 5
  Placement = pos=(0,0,0) rot=(1,0,0;1.5708rad)
  Support = -> [XZ_Plane035]
  sketch-geometry (4):
    g0: LineSegment StartX=-20.2284 StartY=21.3906 StartZ=0 EndX=20.2284 EndY=21.3906 EndZ=0
    g1: LineSegment StartX=20.2284 StartY=21.3906 StartZ=0 EndX=20.2284 EndY=0 EndZ=0
    g2: LineSegment StartX=20.2284 StartY=0 StartZ=0 EndX=-20.2284 EndY=0 EndZ=0
    g3: LineSegment StartX=-20.2284 StartY=0 StartZ=0 EndX=-20.2284 EndY=21.3906 EndZ=0
  constraints (9):
    c: Coincident(g0,g1)
    c: Coincident(g1,g2)
    c: Coincident(g2,g3)
    c: Coincident(g3,g0)
    c: Horizontal(g2)
    c: Vertical(g1)
    c: Vertical(g3)
    c: PointOnObject(g1,g-1)
    c: Symmetric(g0,g0,g-2)
FEATURE [PartDesign::Pad] Pad032
  Direction = (0,-1,-2e-16)
  Length = 5
  Length2 = 10
  Placement = pos=(0,0,0) rot=(1,0,0;1.5708rad)
  Profile = -> Sketch032
  ReferenceAxis = -> Sketch032 [N_Axis]
  Type = 0
FEATURE [PartDesign::Body] Body035
  Group = -> [Sketch032,Pad032]
  Origin = -> Origin035
  Tip = -> Pad032
FEATURE [Part::Cut] Cut027
  Base = -> Body035
  Tool = -> Fusion026
FEATURE [Part::Cylinder] Cylinder024
  Angle = 360
  AttacherType = Attacher::AttachEngine3D
  FirstAngle = 0
  Height = 10
  Placement = pos=(30,22,6) rot=(1,0,0;1.5708rad)
  Radius = 1.1
  SecondAngle = 0
FEATURE [Part::Cylinder] Cylinder025
  Angle = 360
  AttacherType = Attacher::AttachEngine3D
  FirstAngle = 0
  Height = 10
  Placement = pos=(2.2,22,6) rot=(1,0,0;1.5708rad)
  Radius = 1.1
  SecondAngle = 0
FEATURE [Part::MultiFuse] Fusion027  label="tornillosSoporteServoHollo005"
  Shapes = -> [Cylinder025,Cylinder024]
FEATURE [Sketcher::SketchObject] Sketch033
  FullyConstrained = true
  MapMode = 5
  Placement = pos=(0,0,0) rot=(1,0,0;1.5708rad)
  Support = -> [XZ_Plane037]
  expr: Constraints[10] = Spreadsheet.AnchoCuerpoServo
  expr: Constraints[11] = Spreadsheet.LargoTornillosB
  sketch-geometry (4):
    g0: LineSegment StartX=0 StartY=12.5 StartZ=0 EndX=32.5 EndY=12.5 EndZ=0
    g1: LineSegment StartX=32.5 StartY=12.5 StartZ=0 EndX=32.5 EndY=0 EndZ=0
    g2: LineSegment StartX=32.5 StartY=0 StartZ=0 EndX=0 EndY=0 EndZ=0
    g3: LineSegment StartX=0 StartY=0 StartZ=0 EndX=0 EndY=12.5 EndZ=0
  constraints (12):
    c: Coincident(g0,g1)
    c: Coincident(g1,g2)
    c: Coincident(g2,g3)
    c: Coincident(g3,g0)
    c: Horizontal(g0)
    c: Horizontal(g2)
    c: Vertical(g1)
    c: Vertical(g3)
    c: PointOnObject(g0,g-2)
    c: PointOnObject(g1,g-1)
    c: DistanceY(g1,g1) = 12.5
    c: DistanceX(g0,g0) = 32.5
FEATURE [PartDesign::Pad] Pad034
  Direction = (0,-1,-2e-16)
  Length = 4.5
  Length2 = 10
  Placement = pos=(0,0,0) rot=(1,0,0;1.5708rad)
  Profile = -> Sketch033
  ReferenceAxis = -> Sketch033 [N_Axis]
  Type = 0
  expr: Length = Spreadsheet.AltoServoTor
FEATURE [PartDesign::Body] Body037  label="CorteTornillos005"
  Group = -> [Sketch033,Pad034]
  Origin = -> Origin037
  Placement = pos=(0,23,0) rot=(0,0,1;0rad)
  Tip = -> Pad034
FEATURE [Sketcher::SketchObject] Sketch034
  FullyConstrained = false
  MapMode = 5
  Support = -> [XY_Plane036]
  sketch-geometry (4):
    g0: LineSegment StartX=-2.1496 StartY=22.2333 StartZ=0 EndX=33.9123 EndY=22.2333 EndZ=0
    g1: LineSegment StartX=33.9123 StartY=22.2333 StartZ=0 EndX=33.9123 EndY=-3.40604 EndZ=0
    g2: LineSegment StartX=33.9123 StartY=-3.40604 StartZ=0 EndX=-2.1496 EndY=-3.40604 EndZ=0
    g3: LineSegment StartX=-2.1496 StartY=-3.40604 StartZ=0 EndX=-2.1496 EndY=22.2333 EndZ=0
  constraints (8):
    c: Coincident(g0,g1)
    c: Coincident(g1,g2)
    c: Coincident(g2,g3)
    c: Coincident(g3,g0)
    c: Horizontal(g0)
    c: Horizontal(g2)
    c: Vertical(g1)
    c: Vertical(g3)
FEATURE [PartDesign::Pad] Pad033
  Direction = (0,0,1)
  Length = 14
  Length2 = 10
  Profile = -> Sketch034
  ReferenceAxis = -> Sketch034 [N_Axis]
  Type = 0
FEATURE [PartDesign::Body] Body036  label="Base005"
  Group = -> [Sketch034,Pad033]
  Origin = -> Origin036
  Placement = pos=(0,0,-1) rot=(0,0,1;0rad)
  Tip = -> Pad033
FEATURE [Part::Cut] Cut028  label="BaseCorteTornillos005"
  Base = -> Body036
  Tool = -> Body037
FEATURE [Sketcher::SketchObject] Sketch035
  FullyConstrained = true
  MapMode = 5
  Placement = pos=(0,0,0) rot=(1,0,0;1.5708rad)
  Support = -> [XZ_Plane038]
  expr: Constraints[10] = Spreadsheet.LargoCuerpoServo
  expr: Constraints[11] = Spreadsheet.DistanciaBaseO
  expr: Constraints[9] = Spreadsheet.AnchoCuerpoServo
  sketch-geometry (4):
    g0: LineSegment StartX=4.75 StartY=12.5 StartZ=0 EndX=28.05 EndY=12.5 EndZ=0
    g1: LineSegment StartX=28.05 StartY=12.5 StartZ=0 EndX=28.05 EndY=0 EndZ=0
    g2: LineSegment StartX=28.05 StartY=0 StartZ=0 EndX=4.75 EndY=0 EndZ=0
    g3: LineSegment StartX=4.75 StartY=0 StartZ=0 EndX=4.75 EndY=12.5 EndZ=0
  constraints (12):
    c: Coincident(g0,g1)
    c: Coincident(g1,g2)
    c: Coincident(g2,g3)
    c: Coincident(g3,g0)
    c: Horizontal(g0)
    c: Horizontal(g2)
    c: Vertical(g1)
    c: Vertical(g3)
    c: PointOnObject(g1,g-1)
    c: DistanceY(g1,g1) = 12.5
    c: DistanceX(g0,g0) = 23.3
    c: DistanceX(g-1,g2) = 4.75
FEATURE [PartDesign::Pad] Pad035
  Direction = (0,-1,-2e-16)
  Length = 19.5
  Length2 = 10
  Placement = pos=(0,0,0) rot=(1,0,0;1.5708rad)
  Profile = -> Sketch035
  ReferenceAxis = -> Sketch035 [N_Axis]
  Type = 0
  expr: Length = Spreadsheet.AltoServo
FEATURE [PartDesign::Body] Body038  label="CorteCuerpo005"
  Group = -> [Sketch035,Pad035]
  Origin = -> Origin038
  Placement = pos=(0,19,0) rot=(0,0,1;0rad)
  Tip = -> Pad035
FEATURE [Part::Cut] Cut029  label="SoporteServoMG90S005"
  Base = -> Cut028
  Tool = -> Body038
FEATURE [Part::Cut] Cut030  label="SoporteServoCajaMG90S004"
  Base = -> Cut029
  Placement = pos=(-15.5,-9.5,-2.5) rot=(-1,0,0;1.5708rad)
  Tool = -> Fusion027
FEATURE [Part::MultiFuse] Fusion028
  Shapes = -> [Cut030,Cut027]
FEATURE [App::DocumentObjectGroup] Group004  label="Cintura"
  Group = -> [Fusion028]
FEATURE [Part::Box] Box006  label="Cube006"
  AttacherType = Attacher::AttachEngine3D
  Height = 10
  Length = 21
  Placement = pos=(-10.5,-34,0) rot=(0,0,1;0rad)
  Width = 36
FEATURE [Part::Cut] Cut031
  Base = -> Fusion022
  Tool = -> Box006
FEATURE [Part::Feature] ServoGarra_8_001_solid002  label="ServoGarra_8_001 (Solid)002"
  shape: bbox 53.5 x 10 x 23 mm, 482 faces (baked)
FEATURE [Part::Refine] ServoGarra_8_001_solid003  label="ServoGarra_8_001 (Solid)003"
  Source = -> ServoGarra_8_001_solid002
FEATURE [PartDesign::FeatureBase] BaseFeature001
  BaseFeature = -> ServoGarra_8_001_solid003
FEATURE [PartDesign::Body] Body039
  BaseFeature = -> ServoGarra_8_001_solid003
  Group = -> [BaseFeature001]
  Origin = -> Origin039
  Placement = pos=(4.5,0,0) rot=(0,0,1;0rad)
  Tip = -> BaseFeature001
FEATURE [App::DocumentObjectGroup] Group003  label="Cuerpo"
  Group = -> [Cut031,ServoGarra_8_001_solid002,ServoGarra_8_001_solid003,Body039]
